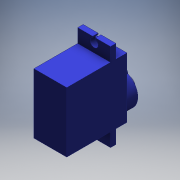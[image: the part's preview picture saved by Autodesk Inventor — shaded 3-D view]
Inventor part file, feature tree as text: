
AUTODESK INVENTOR PART (.ipt)
format: ipt  version: 2016 (Build 200138000, 138)  size: 166,912 bytes
history: native  units: mm
features: extrude x5, sketch x5, other x1, mirror x1
ambient origin geometry x8: Origin, YZ Plane, XZ Plane, XY Plane, X Axis, Y Axis, Z Axis, Center Point
bodies: Body1 (feature_tree)
feature tree (12):
  other  "Sólido1"
  extrude  "Extrusión1"  Depth=5.0mm TaperAngle=0.0deg
  extrude  "Extrusión2"  Depth=4.0mm TaperAngle=0.0deg
  extrude  "Extrusión3"  [1 undecoded]
  mirror  "Simetría1"
  extrude  "Extrusión4"  [1 undecoded]
  extrude  "Extrusión5"  [1 undecoded]
  sketch  "Boceto1"  dims[d2=22.0mm d3=0.0mm d6=5.0mm d7=0.0mm]
  sketch  "Boceto2"  dims[d12=5.0mm d13=0.0mm d19=4.0mm d20=0.0mm]
  sketch  "Boceto3"  dims[d23=3.0mm d24=0.0mm]
  sketch  "Boceto5"
  sketch  "Boceto6"
note: 3 required parameter values undecoded (feature->parameter linkage not recoverable at this tier; creation-order binding heuristic only, values carry confidence <= 0.55)
